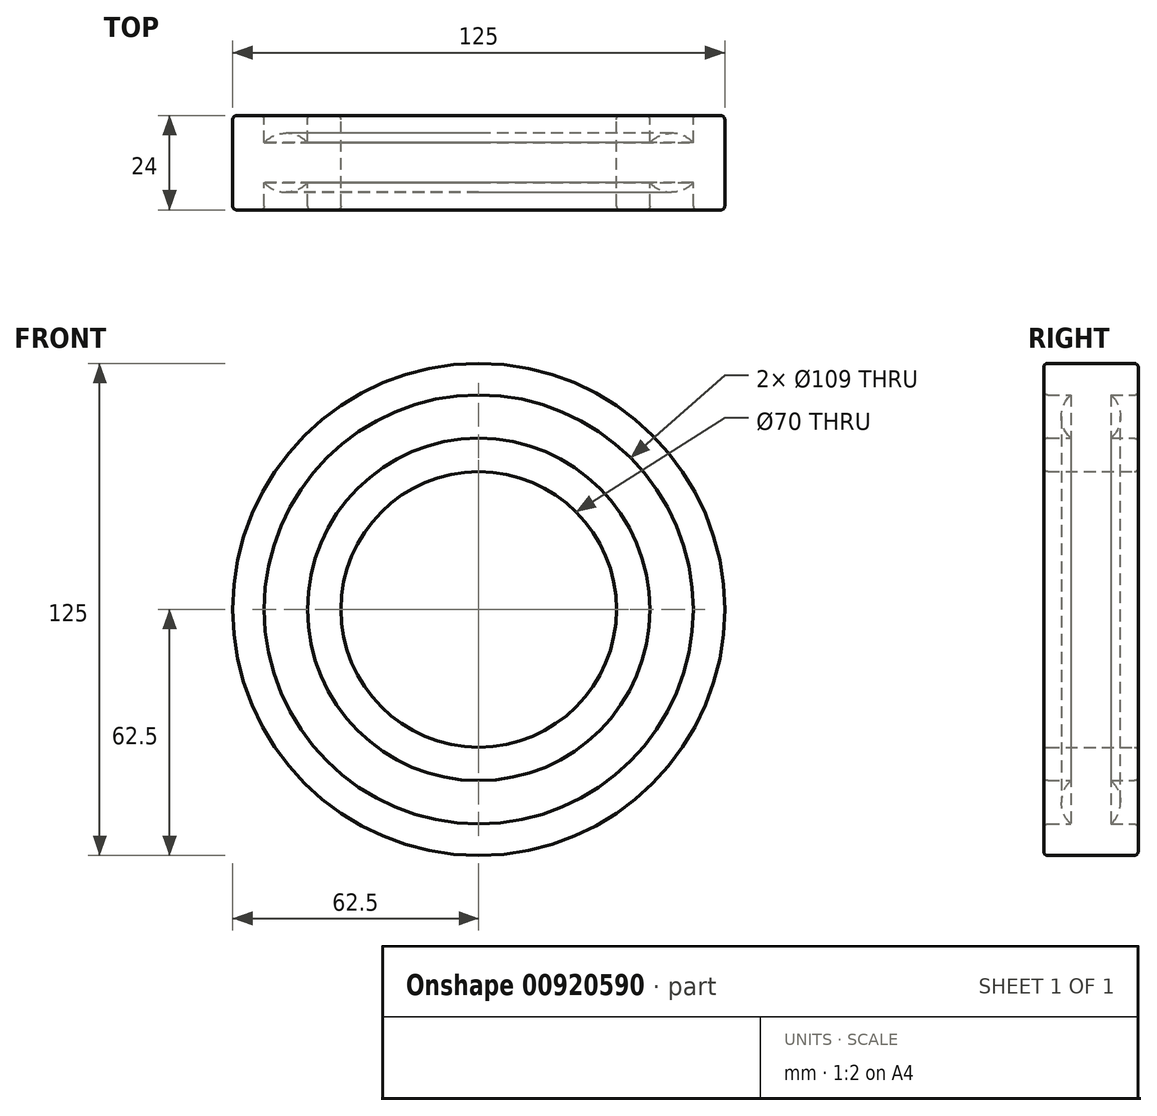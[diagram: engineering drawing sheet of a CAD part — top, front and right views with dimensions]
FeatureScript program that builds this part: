
annotation { "Feature Type Name" : "Feature", "Feature Type Description" : "" }
export const myFeature = defineFeature(function(context is Context, id is Id, definition is map)
    precondition{}
    {
        {
            var Q0;
            Q0=qCreatedBy(makeId("Front.planeOp"),FACE);
            var sketch = newSketch(context, id + "F0", { "sketchPlane" : qUnion([Q0])});
            skCircle(sketch, "E0", {"center": v(0, 0) * mm, "radius": 62.5 * mm});
            skCircle(sketch, "E1", {"center": v(0, 0) * mm, "radius": 35 * mm});
            skSolve(sketch);
        }
        {
            var Q0;
            Q0=makeQuery(id+"F0.imprint","IMPRINT",FACE,{"disambiguationData":[TD([[makeQuery(id+"F0.imprint","IMPRINT",EDGE,{"derivedFrom":sQuery(id+"F0.wireOp",EDGE,"E0")}),1.0]])]});
            extrude(context, id + "F1", {"entities" : qUnion([Q0]), "depth" : 24 * mm, "offsetDistance" : 25 * mm, "symmetric" : true});
        }
        {
            var Q0;
            Q0=qCreatedBy(makeId("Right.planeOp"),FACE);
            var sketch = newSketch(context, id + "F2", { "sketchPlane" : qUnion([Q0])});
            skLineSegment(sketch, "E2", {"start": v(0, 0) * mm, "end": v(32.98, 0) * mm, "construction": true});
            skLineSegment(sketch, "E3.bottom", {"start": v(-22, 54.5) * mm, "end": v(-5.1, 54.5) * mm, "construction": true});
            skLineSegment(sketch, "E3.top", {"start": v(-22, 43.5) * mm, "end": v(-5.1, 43.5) * mm, "construction": true});
            skLineSegment(sketch, "E3.left", {"start": v(-22, 54.5) * mm, "end": v(-22, 43.5) * mm});
            skLineSegment(sketch, "E3.right", {"start": v(22, 54.5) * mm, "end": v(22, 43.5) * mm});
            skLineSegment(sketch, "E4", {"start": v(0, 54.5) * mm, "end": v(0, 43.5) * mm, "construction": true});
            skLineSegment(sketch, "E5", {"start": v(-5.1, 54.5) * mm, "end": v(-22, 54.5) * mm});
            skLineSegment(sketch, "E6", {"start": v(-22, 43.5) * mm, "end": v(-5.1, 43.5) * mm});
            skLineSegment(sketch, "E7", {"start": v(5.1, 54.5) * mm, "end": v(22, 54.5) * mm});
            skLineSegment(sketch, "E8", {"start": v(5.1, 43.5) * mm, "end": v(22, 43.5) * mm});
            skArc(sketch, "E9", {"start": v(-5.1, 54.5) * mm, "mid": v(-7.5, 49) * mm, "end": v(-5.1, 43.5) * mm});
            skLineSegment(sketch, "E10.trimOffspring", {"start": v(5.1, 54.5) * mm, "end": v(22, 54.5) * mm, "construction": true});
            skLineSegment(sketch, "E11.trimOffspring", {"start": v(5.1, 43.5) * mm, "end": v(22, 43.5) * mm, "construction": true});
            skArc(sketch, "E12.trimOffspring", {"start": v(5.1, 43.5) * mm, "mid": v(7.5, 49) * mm, "end": v(5.1, 54.5) * mm});
            skSolve(sketch);
        }
        {
            var Q0;
            Q0=makeQuery(id+"F2.imprint","IMPRINT",FACE,{"disambiguationData":[TD([[makeQuery(id+"F2.imprint","IMPRINT",EDGE,{"derivedFrom":sQuery(id+"F2.wireOp",EDGE,"E3.left")}),1.0]])]});
            var Q1;
            Q1=makeQuery(id+"F2.imprint","IMPRINT",FACE,{"disambiguationData":[TD([[makeQuery(id+"F2.imprint","IMPRINT",EDGE,{"derivedFrom":sQuery(id+"F2.wireOp",EDGE,"E3.right")}),-1.0]])]});
            var Q2;
            Q2=sQuery(id+"F2.wireOp",EDGE,"E2");
            revolve(context, id + "F3", {"operationType" : NewBodyOperationType.REMOVE, "surfaceOperationType" : NewSurfaceOperationType.NEW, "entities" : qUnion([Q0, Q1]), "axis" : qUnion([Q2]), "revolveType" : RevolveType.FULL, "oppositeDirection" : true});
        }
        {
            var Q0;
            Q0=makeQuery(id+"F1.opExtrude","CAP_EDGE",EDGE,{"disambiguationData":[OSD([sQuery(id+"F0.wireOp",EDGE,"E0")])],"isStart":true});
            var Q1;
            Q1=makeQuery(id+"F1.opExtrude","CAP_EDGE",EDGE,{"disambiguationData":[OSD([sQuery(id+"F0.wireOp",EDGE,"E0")])],"isStart":false});
            var Q2;
            Q2=makeQuery(id+"F1.opExtrude","CAP_EDGE",EDGE,{"disambiguationData":[OSD([sQuery(id+"F0.wireOp",EDGE,"E1")])],"isStart":true});
            var Q3;
            Q3=makeQuery(id+"F1.opExtrude","CAP_EDGE",EDGE,{"disambiguationData":[OSD([sQuery(id+"F0.wireOp",EDGE,"E1")])],"isStart":false});
            var Q4;
            Q4=makeQuery(id+"F3.boolean.opBoolean","INTERSECT",EDGE,{"derivedFrom":[makeQuery(id+"F1.opExtrude","CAP_FACE",FACE,{"disambiguationData":[OSD([sQuery(id+"F0.wireOp",EDGE,"E0"),sQuery(id+"F0.wireOp",EDGE,"E1")])],"isStart":false}),makeQuery(id+"F3.opRevolve","SWEPT_FACE",FACE,{"disambiguationData":[OSD([sQuery(id+"F2.wireOp",EDGE,"E5")])]})]});
            var Q5;
            Q5=makeQuery(id+"F3.boolean.opBoolean","INTERSECT",EDGE,{"derivedFrom":[makeQuery(id+"F1.opExtrude","CAP_FACE",FACE,{"disambiguationData":[OSD([sQuery(id+"F0.wireOp",EDGE,"E0"),sQuery(id+"F0.wireOp",EDGE,"E1")])],"isStart":false}),makeQuery(id+"F3.opRevolve","SWEPT_FACE",FACE,{"disambiguationData":[OSD([sQuery(id+"F2.wireOp",EDGE,"E6")])]})]});
            var Q6;
            Q6=makeQuery(id+"F3.boolean.opBoolean","INTERSECT",EDGE,{"derivedFrom":[makeQuery(id+"F1.opExtrude","CAP_FACE",FACE,{"disambiguationData":[OSD([sQuery(id+"F0.wireOp",EDGE,"E0"),sQuery(id+"F0.wireOp",EDGE,"E1")])],"isStart":true}),makeQuery(id+"F3.opRevolve","SWEPT_FACE",FACE,{"disambiguationData":[OSD([sQuery(id+"F2.wireOp",EDGE,"E7")])]})]});
            var Q7;
            Q7=makeQuery(id+"F3.boolean.opBoolean","INTERSECT",EDGE,{"derivedFrom":[makeQuery(id+"F1.opExtrude","CAP_FACE",FACE,{"disambiguationData":[OSD([sQuery(id+"F0.wireOp",EDGE,"E0"),sQuery(id+"F0.wireOp",EDGE,"E1")])],"isStart":true}),makeQuery(id+"F3.opRevolve","SWEPT_FACE",FACE,{"disambiguationData":[OSD([sQuery(id+"F2.wireOp",EDGE,"E8")])]})]});
            fillet(context, id + "F4", {"entities" : qUnion([Q0, Q1, Q2, Q3, Q4, Q5, Q6, Q7]), "radius" : 1 * mm, "tangentPropagation" : true, "allowEdgeOverflow" : false});
        }
    });
